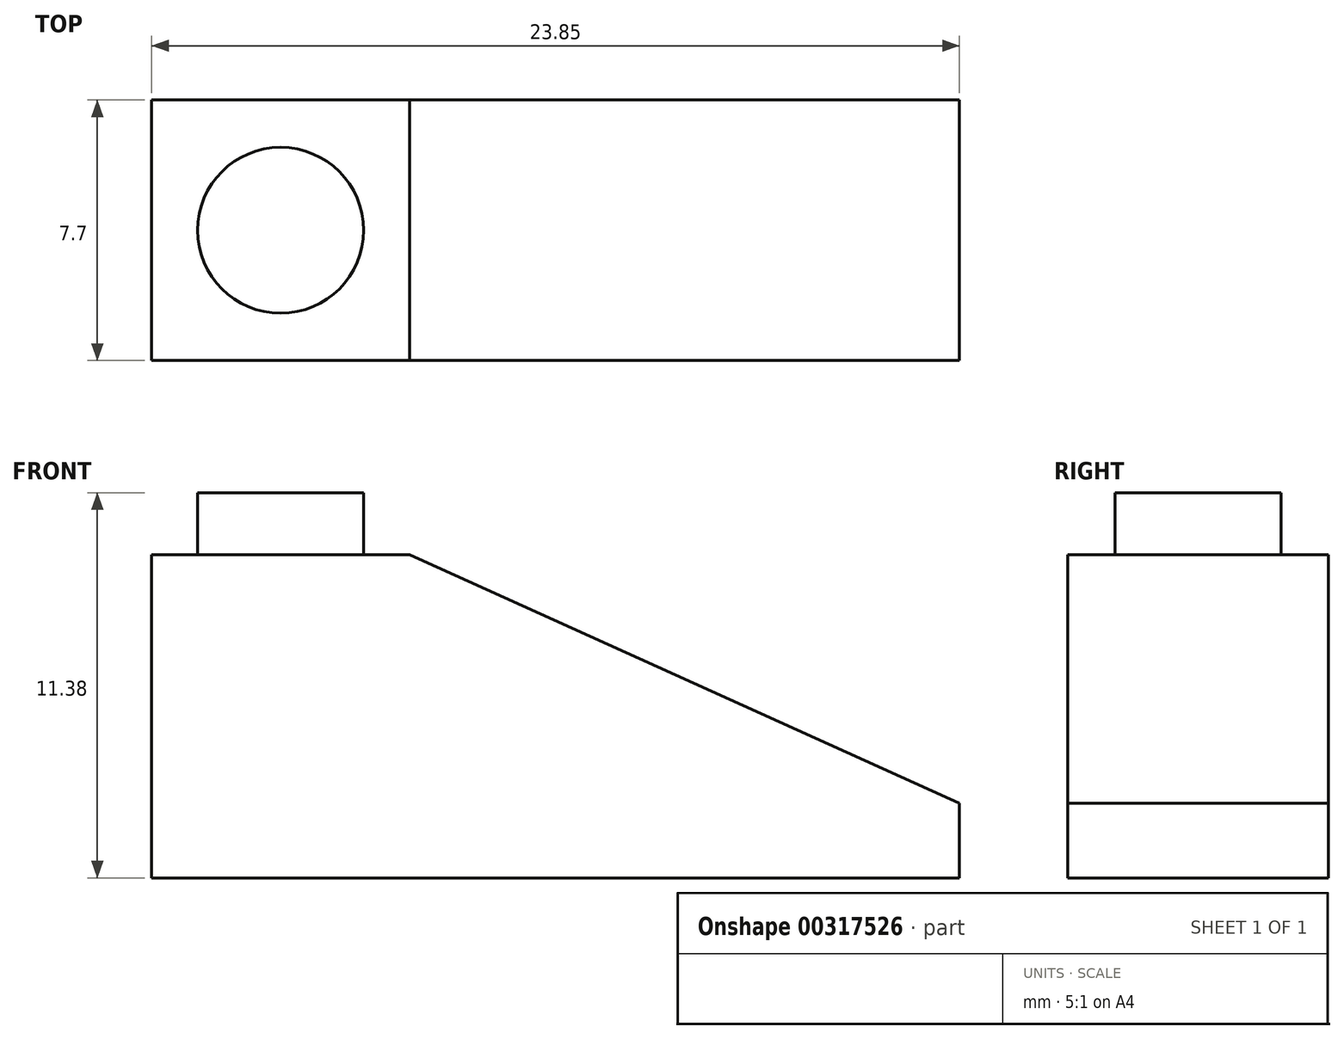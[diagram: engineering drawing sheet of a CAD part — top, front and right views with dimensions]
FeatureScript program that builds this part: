
annotation { "Feature Type Name" : "Feature", "Feature Type Description" : "" }
export const myFeature = defineFeature(function(context is Context, id is Id, definition is map)
    precondition{}
    {
        {
            var Q0;
            Q0=qCreatedBy(makeId("Front.planeOp"),FACE);
            var sketch = newSketch(context, id + "F0", { "sketchPlane" : qUnion([Q0])});
            skLineSegment(sketch, "E0", {"start": v(0, 9.55) * mm, "end": v(7.62, 9.55) * mm});
            skLineSegment(sketch, "E1", {"start": v(7.62, 9.55) * mm, "end": v(7.62, 0) * mm});
            skLineSegment(sketch, "E2", {"start": v(7.62, 0) * mm, "end": v(0, 0) * mm});
            skLineSegment(sketch, "E3", {"start": v(0, 0) * mm, "end": v(0, 9.55) * mm});
            skLineSegment(sketch, "E4", {"start": v(7.62, 9.55) * mm, "end": v(23.85, 2.2) * mm});
            skLineSegment(sketch, "E5", {"start": v(23.85, 2.2) * mm, "end": v(23.85, 0) * mm});
            skLineSegment(sketch, "E6", {"start": v(23.85, 0) * mm, "end": v(7.62, 0) * mm});
            skSolve(sketch);
        }
        {
            var Q0;
            Q0=makeQuery(id+"F0.imprint","IMPRINT",FACE,{"disambiguationData":[TD([[makeQuery(id+"F0.imprint","IMPRINT",EDGE,{"derivedFrom":sQuery(id+"F0.wireOp",EDGE,"E0")}),-1.0]])]});
            var Q1;
            Q1=makeQuery(id+"F0.imprint","IMPRINT",FACE,{"disambiguationData":[TD([[makeQuery(id+"F0.imprint","IMPRINT",EDGE,{"derivedFrom":sQuery(id+"F0.wireOp",EDGE,"E1")}),1.0]])]});
            extrude(context, id + "F1", {"entities" : qUnion([Q0, Q1]), "depth" : 7.7 * mm});
        }
        {
            var Q0;
            Q0=makeQuery(id+"F1.opExtrude","SWEPT_FACE",FACE,{"disambiguationData":[OSD([sQuery(id+"F0.wireOp",EDGE,"E0")])]});
            var sketch = newSketch(context, id + "F2", { "sketchPlane" : qUnion([Q0])});
            skCircle(sketch, "E7", {"center": v(3.81, -3.85) * mm, "radius": 2.45 * mm});
            skPoint(sketch, "E7.centerSnap0", {"position": v(3.81, 0) * mm});
            skPoint(sketch, "E7.centerSnap1", {"position": v(7.62, -3.85) * mm});
            skSolve(sketch);
        }
        {
            var Q0;
            Q0=makeQuery(id+"F2.imprint","IMPRINT",FACE,{"disambiguationData":[TD([[makeQuery(id+"F2.imprint","IMPRINT",EDGE,{"derivedFrom":sQuery(id+"F2.wireOp",EDGE,"E7")}),1.0]])]});
            extrude(context, id + "F3", {"entities" : qUnion([Q0]), "operationType" : NewBodyOperationType.ADD, "depth" : 1.83 * mm});
        }
    });
